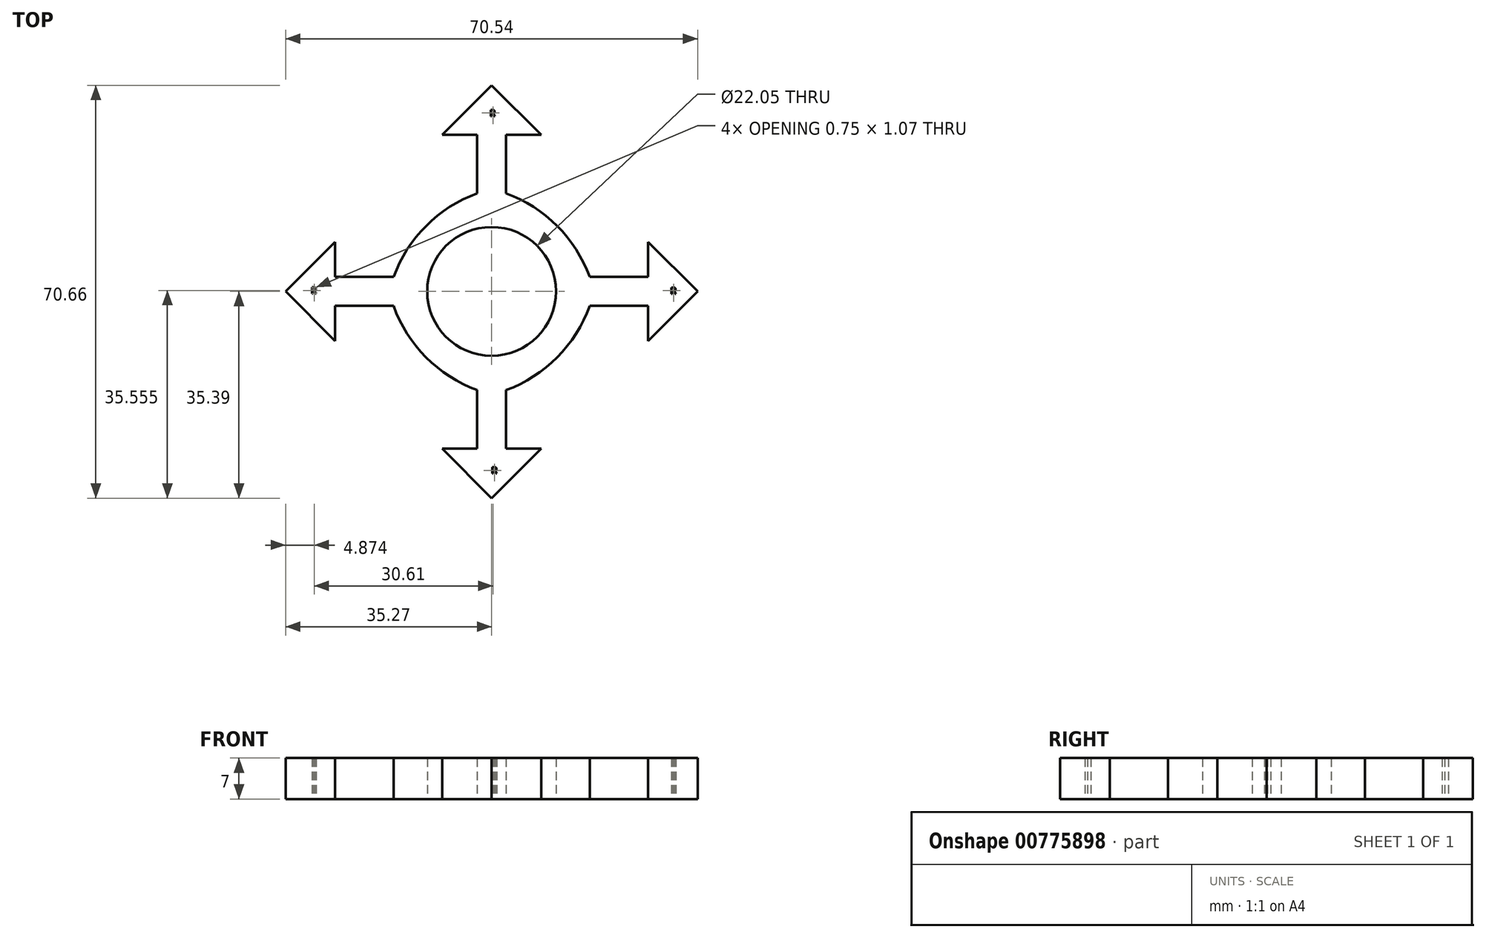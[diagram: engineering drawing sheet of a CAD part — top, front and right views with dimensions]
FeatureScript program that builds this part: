
annotation { "Feature Type Name" : "Feature", "Feature Type Description" : "" }
export const myFeature = defineFeature(function(context is Context, id is Id, definition is map)
    precondition{}
    {
        {
            var Q0;
            Q0=qCreatedBy(makeId("Top.planeOp"),FACE);
            var sketch = newSketch(context, id + "F0", { "sketchPlane" : qUnion([Q0])});
            skLineSegment(sketch, "E0", {"start": v(0, 35.27) * mm, "end": v(-8.49, 26.79) * mm});
            skLineSegment(sketch, "E1", {"start": v(0, 35.27) * mm, "end": v(8.49, 26.79) * mm});
            skLineSegment(sketch, "E2", {"start": v(-8.49, 26.79) * mm, "end": v(-2.49, 26.79) * mm});
            skLineSegment(sketch, "E3", {"start": v(8.49, 26.79) * mm, "end": v(2.49, 26.79) * mm});
            skLineSegment(sketch, "E4", {"start": v(-2.49, 26.79) * mm, "end": v(-2.49, 16.79) * mm});
            skLineSegment(sketch, "E5", {"start": v(2.49, 26.79) * mm, "end": v(2.49, 16.79) * mm});
            skLineSegment(sketch, "E6", {"start": v(35.27, 0) * mm, "end": v(26.79, 8.49) * mm});
            skLineSegment(sketch, "E7", {"start": v(35.27, 0) * mm, "end": v(26.79, -8.49) * mm});
            skLineSegment(sketch, "E8", {"start": v(26.79, 8.49) * mm, "end": v(26.79, 2.49) * mm});
            skLineSegment(sketch, "E9", {"start": v(26.79, -8.49) * mm, "end": v(26.79, -2.49) * mm});
            skLineSegment(sketch, "E10", {"start": v(26.79, 2.49) * mm, "end": v(16.79, 2.49) * mm});
            skLineSegment(sketch, "E11", {"start": v(26.79, -2.49) * mm, "end": v(16.79, -2.49) * mm});
            skLineSegment(sketch, "E12", {"start": v(0, -35.39) * mm, "end": v(8.49, -26.9) * mm});
            skLineSegment(sketch, "E13", {"start": v(0, -35.39) * mm, "end": v(-8.49, -26.9) * mm});
            skLineSegment(sketch, "E14", {"start": v(8.49, -26.9) * mm, "end": v(2.49, -26.9) * mm});
            skLineSegment(sketch, "E15", {"start": v(-8.49, -26.9) * mm, "end": v(-2.49, -26.9) * mm});
            skLineSegment(sketch, "E16", {"start": v(2.49, -26.9) * mm, "end": v(2.49, -16.9) * mm});
            skLineSegment(sketch, "E17", {"start": v(-2.49, -26.9) * mm, "end": v(-2.49, -16.9) * mm});
            skLineSegment(sketch, "E18", {"start": v(-35.27, 0) * mm, "end": v(-26.79, -8.49) * mm});
            skLineSegment(sketch, "E19", {"start": v(-35.27, 0) * mm, "end": v(-26.79, 8.49) * mm});
            skLineSegment(sketch, "E20", {"start": v(-26.79, -8.49) * mm, "end": v(-26.79, -2.49) * mm});
            skLineSegment(sketch, "E21", {"start": v(-26.79, 8.49) * mm, "end": v(-26.79, 2.49) * mm});
            skLineSegment(sketch, "E22", {"start": v(-26.79, -2.49) * mm, "end": v(-16.79, -2.49) * mm});
            skLineSegment(sketch, "E23", {"start": v(-26.79, 2.49) * mm, "end": v(-16.79, 2.49) * mm});
            skCircle(sketch, "E24", {"center": v(0, 0) * mm, "radius": 11.03 * mm});
            skArc(sketch, "E25", {"start": v(-16.79, -2.49) * mm, "mid": v(-11.24, -11.28) * mm, "end": v(-2.49, -16.9) * mm});
            skArc(sketch, "E26", {"start": v(-2.49, 16.79) * mm, "mid": v(-11.22, 11.22) * mm, "end": v(-16.79, 2.49) * mm});
            skArc(sketch, "E27", {"start": v(16.79, 2.49) * mm, "mid": v(11.22, 11.22) * mm, "end": v(2.49, 16.79) * mm});
            skArc(sketch, "E28", {"start": v(2.49, -16.9) * mm, "mid": v(11.24, -11.28) * mm, "end": v(16.79, -2.49) * mm});
            skText(sketch, "E29", { "text": "R", "fontName": "OpenSans-Regular.ttf"});
            skText(sketch, "E30", { "text": "R", "fontName": "OpenSans-Regular.ttf"});
            skText(sketch, "E31", { "text": "R", "fontName": "OpenSans-Regular.ttf"});
            skText(sketch, "E32", { "text": "R\n", "fontName": "OpenSans-Regular.ttf"});
            const initialGuessF0  = {"E29": [-0.00031, 0.03, 1, 0, 0.00108], "E30": [0.03066, -0.0004, 1, 0, 0.00108], "E31": [0, -0.03116, 1, 0, 0.00108], "E32": [-0.03092, -0.00037, 1, 0, 0.00108]};
            skSetInitialGuess(sketch, initialGuessF0);
            skSolve(sketch);
        }
        {
            var Q0;
            Q0 = qSketchRegion(id + "F0", true);
            extrude(context, id + "F1", {"entities" : qUnion([Q0]), "depth" : 7 * mm, "offsetDistance" : 25 * mm});
        }
    });
